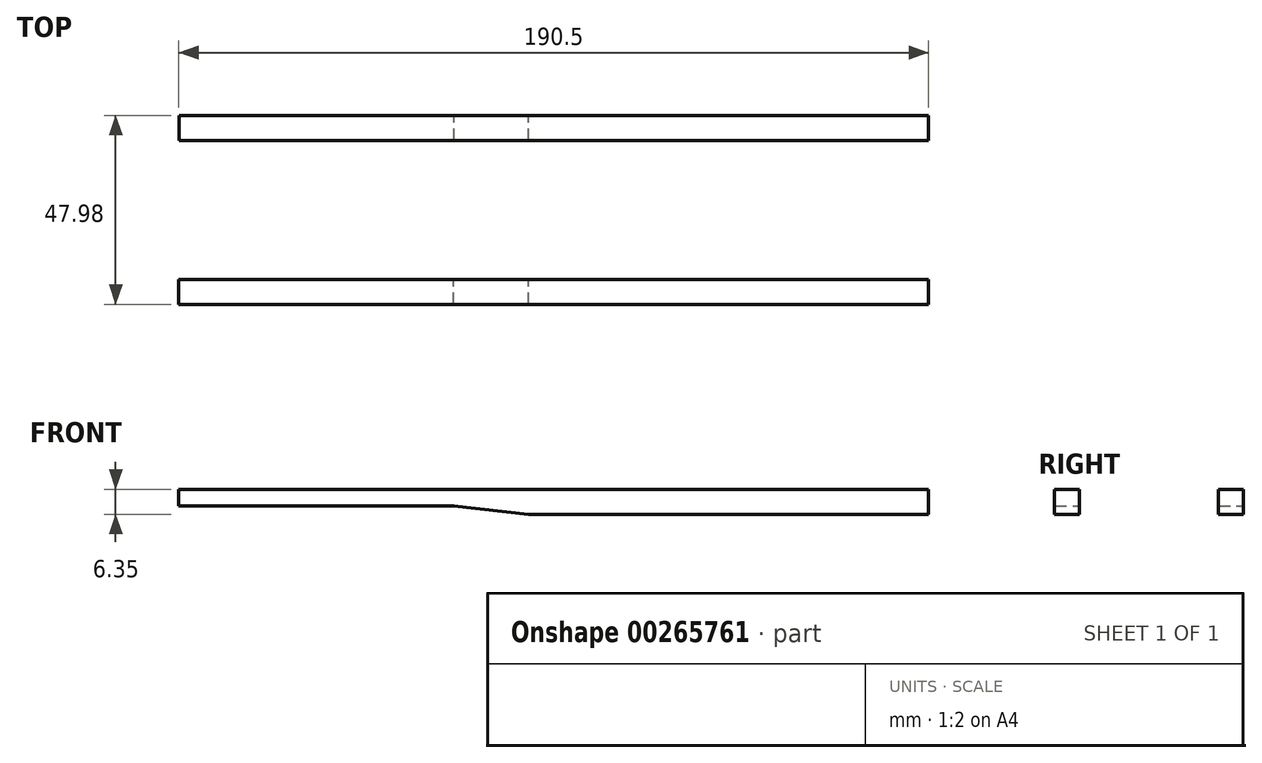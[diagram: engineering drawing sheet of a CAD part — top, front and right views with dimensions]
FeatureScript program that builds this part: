
annotation { "Feature Type Name" : "Feature", "Feature Type Description" : "" }
export const myFeature = defineFeature(function(context is Context, id is Id, definition is map)
    precondition{}
    {
        {
            var Q0;
            Q0=qCreatedBy(makeId("Right.planeOp"),FACE);
            var sketch = newSketch(context, id + "F0", { "sketchPlane" : qUnion([Q0])});
            skLineSegment(sketch, "E0", {"start": v(-23.99, 4.18) * mm, "end": v(-23.99, -2.17) * mm});
            skLineSegment(sketch, "E1", {"start": v(-23.99, -2.17) * mm, "end": v(-17.64, -2.17) * mm});
            skLineSegment(sketch, "E2", {"start": v(-17.64, -2.17) * mm, "end": v(-17.64, 4.18) * mm});
            skLineSegment(sketch, "E3", {"start": v(-17.64, 4.18) * mm, "end": v(-23.99, 4.18) * mm});
            skLineSegment(sketch, "E4", {"start": v(17.64, 4.18) * mm, "end": v(17.64, -2.17) * mm});
            skLineSegment(sketch, "E5", {"start": v(17.64, -2.17) * mm, "end": v(23.99, -2.17) * mm});
            skLineSegment(sketch, "E6", {"start": v(23.99, -2.17) * mm, "end": v(23.99, 4.18) * mm});
            skLineSegment(sketch, "E7", {"start": v(23.99, 4.18) * mm, "end": v(17.64, 4.18) * mm});
            skSolve(sketch);
        }
        {
            var Q0;
            Q0=makeQuery(id+"F0.imprint","IMPRINT",FACE,{"disambiguationData":[TD([[makeQuery(id+"F0.imprint","IMPRINT",EDGE,{"derivedFrom":sQuery(id+"F0.wireOp",EDGE,"E0")}),1.0]])]});
            var Q1;
            Q1=makeQuery(id+"F0.imprint","IMPRINT",FACE,{"disambiguationData":[TD([[makeQuery(id+"F0.imprint","IMPRINT",EDGE,{"derivedFrom":sQuery(id+"F0.wireOp",EDGE,"E4")}),1.0]])]});
            extrude(context, id + "F1", {"entities" : qUnion([Q0, Q1]), "depth" : 101.6 * mm});
        }
        {
            var Q0;
            Q0=makeQuery(id+"F1.opExtrude","SWEPT_FACE",FACE,{"disambiguationData":[OSD([sQuery(id+"F0.wireOp",EDGE,"E2")])]});
            var sketch = newSketch(context, id + "F2", { "sketchPlane" : qUnion([Q0])});
            skLineSegment(sketch, "E8", {"start": v(0, 4.18) * mm, "end": v(88.9, 4.18) * mm});
            skLineSegment(sketch, "E9", {"start": v(88.9, 4.18) * mm, "end": v(88.9, 0) * mm});
            skLineSegment(sketch, "E10", {"start": v(88.9, 0) * mm, "end": v(19.05, 0) * mm});
            skLineSegment(sketch, "E11", {"start": v(19.05, 0) * mm, "end": v(0, -2.17) * mm});
            skSolve(sketch);
        }
        {
            var Q0;
            Q0=makeQuery(id+"F2.imprint","IMPRINT",FACE,{"disambiguationData":[TD([[makeQuery(id+"F2.imprint","IMPRINT",EDGE,{"derivedFrom":sQuery(id+"F2.wireOp",EDGE,"E8")}),-1.0]])]});
            extrude(context, id + "F3", {"entities" : qUnion([Q0]), "operationType" : NewBodyOperationType.ADD, "oppositeDirection" : true, "depth" : 6.35 * mm});
        }
        {
            var Q0;
            Q0=makeQuery(id+"F1.opExtrude","SWEPT_FACE",FACE,{"disambiguationData":[OSD([sQuery(id+"F0.wireOp",EDGE,"E6")])]});
            var sketch = newSketch(context, id + "F4", { "sketchPlane" : qUnion([Q0])});
            skLineSegment(sketch, "E12", {"start": v(0, 4.18) * mm, "end": v(88.78, 4.18) * mm});
            skLineSegment(sketch, "E13", {"start": v(88.78, 4.18) * mm, "end": v(88.78, 0) * mm});
            skLineSegment(sketch, "E14", {"start": v(18.93, -0.01) * mm, "end": v(0, -2.17) * mm});
            skLineSegment(sketch, "E15", {"start": v(0, -2.17) * mm, "end": v(-101.6, -2.17) * mm});
            skLineSegment(sketch, "E16", {"start": v(-101.6, -2.17) * mm, "end": v(-101.6, 4.18) * mm});
            skLineSegment(sketch, "E17", {"start": v(18.93, -0.01) * mm, "end": v(88.78, 0) * mm});
            skSolve(sketch);
        }
        {
            var Q0;
            Q0=makeQuery(id+"F4.imprint","IMPRINT",FACE,{"disambiguationData":[TD([[makeQuery(id+"F4.imprint","IMPRINT",EDGE,{"derivedFrom":sQuery(id+"F4.wireOp",EDGE,"E12")}),-1.0]])]});
            extrude(context, id + "F5", {"entities" : qUnion([Q0]), "operationType" : NewBodyOperationType.ADD, "oppositeDirection" : true, "depth" : 6.35 * mm});
        }
    });
